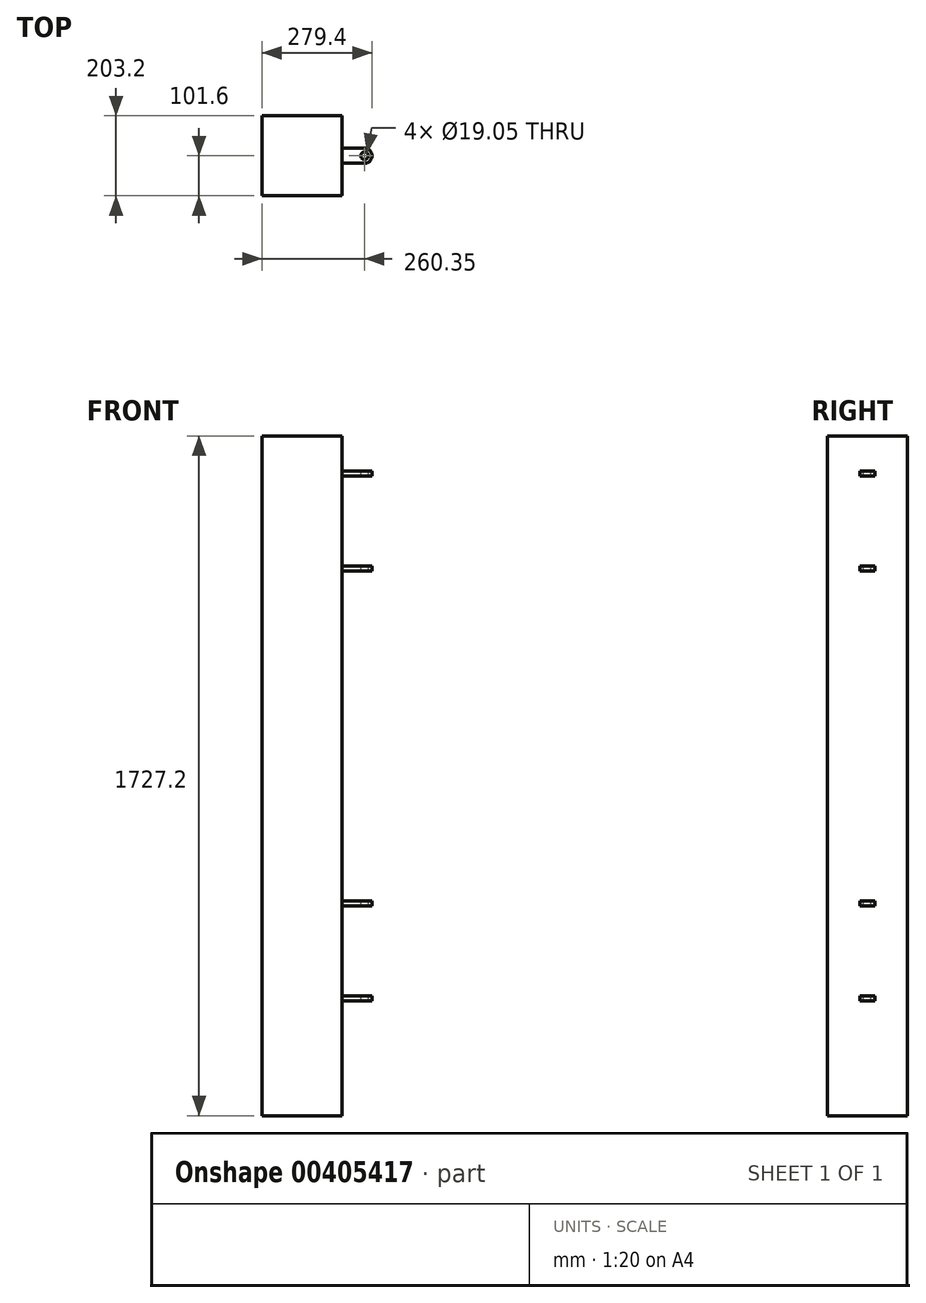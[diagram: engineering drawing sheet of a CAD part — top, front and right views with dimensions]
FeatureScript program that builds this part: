
annotation { "Feature Type Name" : "Feature", "Feature Type Description" : "" }
export const myFeature = defineFeature(function(context is Context, id is Id, definition is map)
    precondition{}
    {
        {
            var Q0;
            Q0=qCreatedBy(makeId("Front.planeOp"),FACE);
            var sketch = newSketch(context, id + "F0", { "sketchPlane" : qUnion([Q0])});
            skLineSegment(sketch, "E0.bottom", {"start": v(-101.6, 863.6) * mm, "end": v(101.6, 863.6) * mm});
            skLineSegment(sketch, "E0.top", {"start": v(-101.6, -863.6) * mm, "end": v(101.6, -863.6) * mm});
            skLineSegment(sketch, "E0.left", {"start": v(-101.6, 863.6) * mm, "end": v(-101.6, -863.6) * mm});
            skLineSegment(sketch, "E0.right", {"start": v(101.6, 863.6) * mm, "end": v(101.6, -863.6) * mm});
            skSolve(sketch);
        }
        {
            var Q0;
            Q0=makeQuery(id+"F0.imprint","IMPRINT",FACE,{"disambiguationData":[TD([[makeQuery(id+"F0.imprint","IMPRINT",EDGE,{"derivedFrom":sQuery(id+"F0.wireOp",EDGE,"E0.bottom")}),-1.0]])]});
            extrude(context, id + "F1", {"entities" : qUnion([Q0]), "depth" : 203.2 * mm, "symmetric" : true});
        }
        {
            var Q0;
            Q0=makeQuery(id+"F1.opExtrude","SWEPT_FACE",FACE,{"disambiguationData":[OSD([sQuery(id+"F0.wireOp",EDGE,"E0.right")])]});
            var sketch = newSketch(context, id + "F2", { "sketchPlane" : qUnion([Q0])});
            skLineSegment(sketch, "E1.bottom", {"start": v(-19.05, 774.7) * mm, "end": v(19.05, 774.7) * mm});
            skLineSegment(sketch, "E1.top", {"start": v(-19.05, 762) * mm, "end": v(19.05, 762) * mm});
            skLineSegment(sketch, "E1.left", {"start": v(-19.05, 774.7) * mm, "end": v(-19.05, 762) * mm});
            skLineSegment(sketch, "E1.right", {"start": v(19.05, 774.7) * mm, "end": v(19.05, 762) * mm});
            skLineSegment(sketch, "E2.bottom", {"start": v(-19.05, 533.4) * mm, "end": v(19.05, 533.4) * mm});
            skLineSegment(sketch, "E2.top", {"start": v(-19.05, 520.7) * mm, "end": v(19.05, 520.7) * mm});
            skLineSegment(sketch, "E2.left", {"start": v(-19.05, 533.4) * mm, "end": v(-19.05, 520.7) * mm});
            skLineSegment(sketch, "E2.right", {"start": v(19.05, 533.4) * mm, "end": v(19.05, 520.7) * mm});
            skLineSegment(sketch, "E3.bottom", {"start": v(-19.05, -317.5) * mm, "end": v(19.05, -317.5) * mm});
            skLineSegment(sketch, "E3.top", {"start": v(-19.05, -330.2) * mm, "end": v(19.05, -330.2) * mm});
            skLineSegment(sketch, "E3.left", {"start": v(-19.05, -317.5) * mm, "end": v(-19.05, -330.2) * mm});
            skLineSegment(sketch, "E3.right", {"start": v(19.05, -317.5) * mm, "end": v(19.05, -330.2) * mm});
            skLineSegment(sketch, "E4.bottom", {"start": v(-19.05, -558.8) * mm, "end": v(19.05, -558.8) * mm});
            skLineSegment(sketch, "E4.top", {"start": v(-19.05, -571.5) * mm, "end": v(19.05, -571.5) * mm});
            skLineSegment(sketch, "E4.left", {"start": v(-19.05, -558.8) * mm, "end": v(-19.05, -571.5) * mm});
            skLineSegment(sketch, "E4.right", {"start": v(19.05, -558.8) * mm, "end": v(19.05, -571.5) * mm});
            skSolve(sketch);
        }
        {
            var Q0;
            Q0=makeQuery(id+"F2.imprint","IMPRINT",FACE,{"disambiguationData":[TD([[makeQuery(id+"F2.imprint","IMPRINT",EDGE,{"derivedFrom":sQuery(id+"F2.wireOp",EDGE,"E4.bottom")}),-1.0]])]});
            var Q1;
            Q1=makeQuery(id+"F2.imprint","IMPRINT",FACE,{"disambiguationData":[TD([[makeQuery(id+"F2.imprint","IMPRINT",EDGE,{"derivedFrom":sQuery(id+"F2.wireOp",EDGE,"E3.bottom")}),-1.0]])]});
            var Q2;
            Q2=makeQuery(id+"F2.imprint","IMPRINT",FACE,{"disambiguationData":[TD([[makeQuery(id+"F2.imprint","IMPRINT",EDGE,{"derivedFrom":sQuery(id+"F2.wireOp",EDGE,"E2.bottom")}),-1.0]])]});
            var Q3;
            Q3=makeQuery(id+"F2.imprint","IMPRINT",FACE,{"disambiguationData":[TD([[makeQuery(id+"F2.imprint","IMPRINT",EDGE,{"derivedFrom":sQuery(id+"F2.wireOp",EDGE,"E1.bottom")}),-1.0]])]});
            extrude(context, id + "F3", {"entities" : qUnion([Q0, Q1, Q2, Q3]), "operationType" : NewBodyOperationType.ADD, "depth" : 76.2 * mm});
        }
        {
            var Q0;
            Q0=makeQuery(id+"F3.opExtrude","CAP_EDGE",EDGE,{"disambiguationData":[OSD([sQuery(id+"F2.wireOp",EDGE,"E4.right")])],"isStart":false});
            var Q1;
            Q1=makeQuery(id+"F3.opExtrude","CAP_EDGE",EDGE,{"disambiguationData":[OSD([sQuery(id+"F2.wireOp",EDGE,"E4.left")])],"isStart":false});
            var Q2;
            Q2=makeQuery(id+"F3.opExtrude","CAP_EDGE",EDGE,{"disambiguationData":[OSD([sQuery(id+"F2.wireOp",EDGE,"E3.right")])],"isStart":false});
            var Q3;
            Q3=makeQuery(id+"F3.opExtrude","CAP_EDGE",EDGE,{"disambiguationData":[OSD([sQuery(id+"F2.wireOp",EDGE,"E3.left")])],"isStart":false});
            var Q4;
            Q4=makeQuery(id+"F3.opExtrude","CAP_EDGE",EDGE,{"disambiguationData":[OSD([sQuery(id+"F2.wireOp",EDGE,"E2.right")])],"isStart":false});
            var Q5;
            Q5=makeQuery(id+"F3.opExtrude","CAP_EDGE",EDGE,{"disambiguationData":[OSD([sQuery(id+"F2.wireOp",EDGE,"E2.left")])],"isStart":false});
            var Q6;
            Q6=makeQuery(id+"F3.opExtrude","CAP_EDGE",EDGE,{"disambiguationData":[OSD([sQuery(id+"F2.wireOp",EDGE,"E1.right")])],"isStart":false});
            var Q7;
            Q7=makeQuery(id+"F3.opExtrude","CAP_EDGE",EDGE,{"disambiguationData":[OSD([sQuery(id+"F2.wireOp",EDGE,"E1.left")])],"isStart":false});
            fillet(context, id + "F4", {"entities" : qUnion([Q0, Q1, Q2, Q3, Q4, Q5, Q6, Q7]), "radius" : 19.05 * mm, "tangentPropagation" : true, "allowEdgeOverflow" : false});
        }
        {
            var Q0;
            Q0=makeQuery(id+"F3.opExtrude","SWEPT_FACE",FACE,{"disambiguationData":[OSD([sQuery(id+"F2.wireOp",EDGE,"E1.bottom")])]});
            var sketch = newSketch(context, id + "F5", { "sketchPlane" : qUnion([Q0])});
            skCircle(sketch, "E5", {"center": v(158.75, 0) * mm, "radius": 9.53 * mm});
            skSolve(sketch);
        }
        {
            var Q0;
            Q0=makeQuery(id+"F5.imprint","IMPRINT",FACE,{"disambiguationData":[TD([[makeQuery(id+"F5.imprint","IMPRINT",EDGE,{"derivedFrom":sQuery(id+"F5.wireOp",EDGE,"E5")}),1.0]])]});
            extrude(context, id + "F6", {"entities" : qUnion([Q0]), "operationType" : NewBodyOperationType.REMOVE, "endBound" : BoundingType.THROUGH_ALL, "oppositeDirection" : true, "depth" : 25.4 * mm});
        }
    });
